# Revit family: HERZ Strömax полиамид, цвет маховика - зеленый 4217 GN
name_source: partatom
category: Rohrzubehör
units: mm (PartAtom-declared; Revit-internal decimal feet)

## family parameters
Arbeitsebenenbasiert = Nein
Beim Laden mit Abzugskörper schneiden = Nein
Bemaßung runder Anschluss = Durchmesser verwenden
Gemeinsam genutzt = Nein
Immer vertikal = Ja
OmniClass-Nummer = 23.65.55.14
OmniClass-Titel = Valves for Liquid Services
Teiletyp = Unterbricht

## types (1)
- HERZ Strömax полиамид, цвет маховика - зеленый 4217 GN
    D04 = 16.25 mm  [stored 0.0533136 ft]
    D05 = 16.75 mm
    H01 = 41.5 mm
    Hersteller = HERZ Armaturen Ges.m.b.H.
    MD01 = 7.4 mm  [stored 0.0242782 ft]
    S02 = 60 mm  [stored 0.19685 ft]
    SCRNCODE = 05;07;02
    SCRNSEQ = ARM;ARM_TYP="STRV";2
    SC_NennweiteBerechnet = 0
    URL = www.herz-armaturen.ru
    W01 = 30.00°
    W02 = 60.00°
    Внутренняя резьба = в соответствии с ISO 7/1
    Измерение перепада давления = Клапаны STRÖMAX-GN оснащены двумя измерительными клапанами:
с помощью измерительного прибора можно измерить перепад давления и по нему определить текущий расход в зависимости от степени преднастройки.
HERZ Измерительный компьютер (1 8900 05) позволяет напрямую считывать расход (см. руководство к измерительным приборам).
    Исполнение = STRÖMAX-GN Балансировочный клапан с равнопроцентной пропускной характеристикой, с измерительными клапанами, 1/2′′ – 2′′.
Исполнение с прямым невыдвижным шпинделем, муфта х муфта, латунный корпус без покрытия, уплотнение шпинделя двойным кольцевым уплотнением O-Ring, преднастройка посредством ограничения хода внутреннего шпинделя, шкала настройки находится на корпусе маховика.
Два измерительных клапана расположены рядом с маховиком.
    Корпус = латунь CW602N
    Макс. рабочая температура (до DN32) = 130 °C
    Макс. рабочая температура (с DN40) = 110 °C
    Макс. рабочее давление = 2500000.0 Pa
    Маховик = полиамид, цвет маховика - красный
    Область применения = Балансировочные клапаны применяются для гидравлической балансировки систем отопления и охлаждения, регулировки магистральных трубопроводов, стояков, теплообменников, регистров отопления и охлаждения.
    Положение клапана при монтаже = Неподнимающийся шпиндель, расположенный перпендикулярно оси клапана, обеспечивает доступность и лёгкость в обслуживании в любом монтажном положении.
    Среда = Качество теплоносителя в соответствии с ÖNORM H5195 и VDI 2035.
Допускается использование этилен- и пропиленгликоля в соотношении 25-50 % с водой.
    Уплотнение шпинделя = EPDM
    Шпиндель = латунь CW617N

note: [stored X ft] marks values corroborated as IEEE doubles in the binary element streams (Revit-internal decimal feet)
